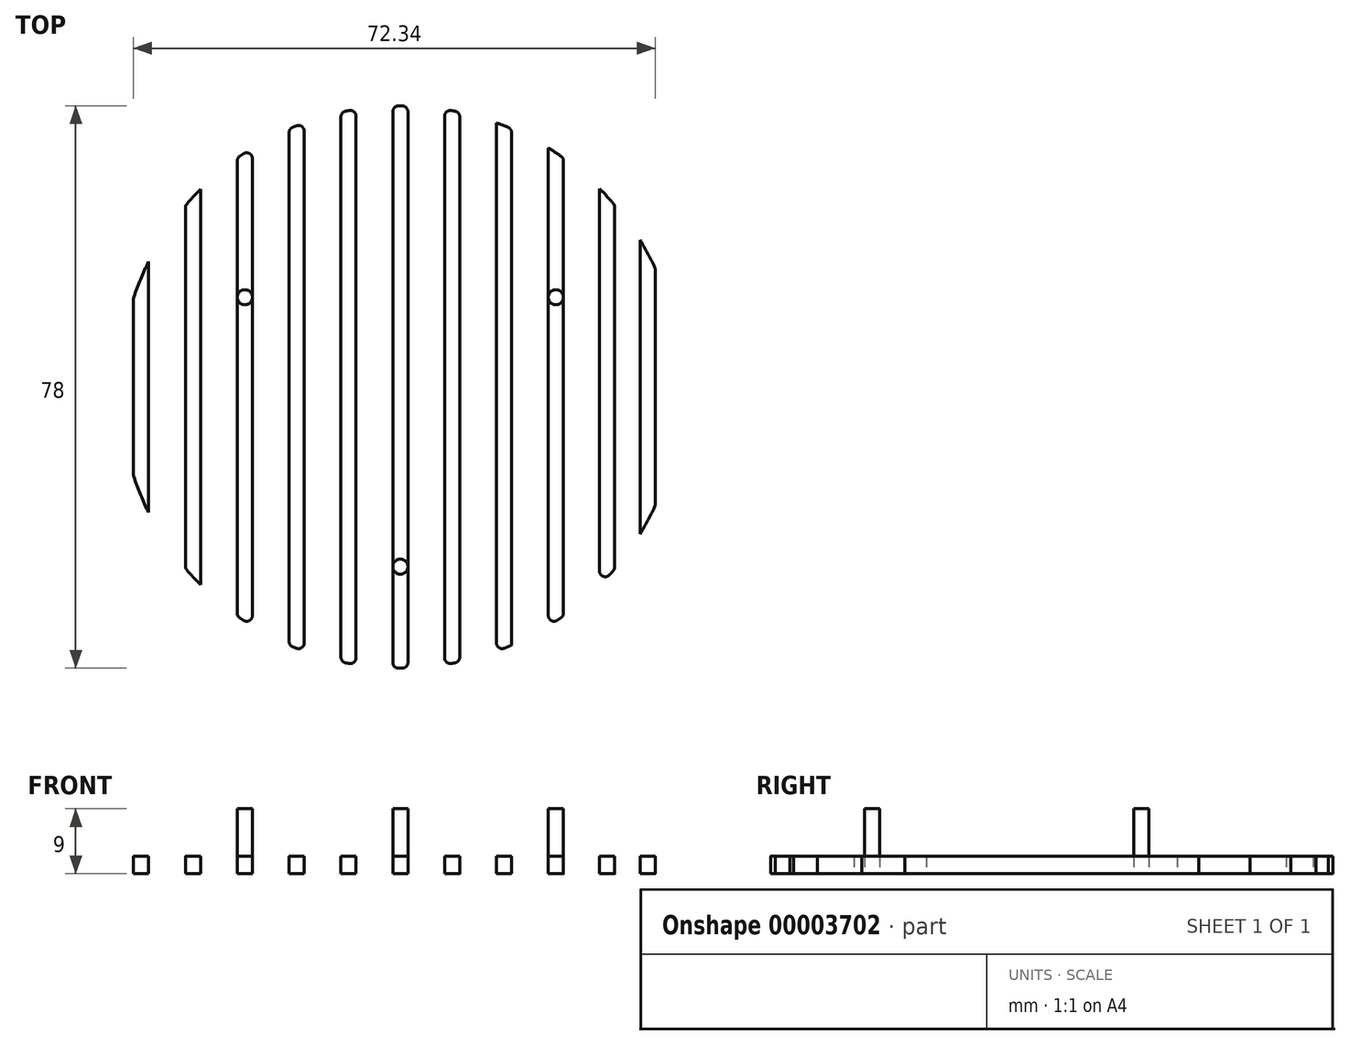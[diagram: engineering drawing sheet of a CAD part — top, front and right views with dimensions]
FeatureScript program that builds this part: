
annotation { "Feature Type Name" : "Feature", "Feature Type Description" : "" }
export const myFeature = defineFeature(function(context is Context, id is Id, definition is map)
    precondition{}
    {
        {
            var Q0;
            Q0=qCreatedBy(makeId("Top.planeOp"),FACE);
            var sketch = newSketch(context, id + "F0", { "sketchPlane" : qUnion([Q0])});
            skCircle(sketch, "E0", {"center": v(0, 0) * mm, "radius": 39 * mm});
            skCircle(sketch, "E1", {"center": v(0, -24.91) * mm, "radius": 1.05 * mm});
            skCircle(sketch, "E2.1.0", {"center": v(21.57, 12.46) * mm, "radius": 1.05 * mm});
            skCircle(sketch, "E2.2.0", {"center": v(-21.57, 12.46) * mm, "radius": 1.05 * mm});
            skLineSegment(sketch, "E3", {"start": v(-1.05, -24.91) * mm, "end": v(-1.05, 38.99) * mm});
            skLineSegment(sketch, "E4", {"start": v(1.05, -24.91) * mm, "end": v(1.05, 38.99) * mm});
            skLineSegment(sketch, "E5", {"start": v(-1.05, -24.91) * mm, "end": v(-1.05, -38.99) * mm});
            skLineSegment(sketch, "E6", {"start": v(1.05, -24.91) * mm, "end": v(1.05, -38.99) * mm});
            skLineSegment(sketch, "E7", {"start": v(-22.62, 12.46) * mm, "end": v(-22.62, 31.77) * mm});
            skLineSegment(sketch, "E8", {"start": v(-20.52, 12.46) * mm, "end": v(-20.52, 33.16) * mm});
            skLineSegment(sketch, "E9", {"start": v(-22.62, 12.46) * mm, "end": v(-22.62, -31.77) * mm});
            skLineSegment(sketch, "E10", {"start": v(-20.52, 12.46) * mm, "end": v(-20.52, -33.16) * mm});
            skLineSegment(sketch, "E11", {"start": v(-20.52, -33.16) * mm, "end": v(-19.7, -33.83) * mm});
            skLineSegment(sketch, "E12", {"start": v(20.52, 12.46) * mm, "end": v(20.52, 33.16) * mm});
            skLineSegment(sketch, "E13", {"start": v(22.62, 12.46) * mm, "end": v(22.62, 31.77) * mm});
            skLineSegment(sketch, "E14", {"start": v(20.52, 12.46) * mm, "end": v(20.52, -33.16) * mm});
            skLineSegment(sketch, "E15", {"start": v(22.62, 12.46) * mm, "end": v(22.62, -31.77) * mm});
            skCircle(sketch, "E16", {"center": v(0, 0) * mm, "radius": 41.1 * mm});
            skLineSegment(sketch, "E17", {"start": v(-15.43, 35.82) * mm, "end": v(-15.43, -35.82) * mm});
            skLineSegment(sketch, "E18", {"start": v(-13.33, 36.65) * mm, "end": v(-13.33, -36.65) * mm});
            skLineSegment(sketch, "E19", {"start": v(-8.24, 38.12) * mm, "end": v(-8.24, -38.12) * mm});
            skLineSegment(sketch, "E20", {"start": v(-6.14, 38.51) * mm, "end": v(-6.14, -38.12) * mm});
            skLineSegment(sketch, "E21", {"start": v(-20.52, 0) * mm, "end": v(-15.43, 0) * mm});
            skLineSegment(sketch, "E22", {"start": v(-13.33, 0) * mm, "end": v(-8.24, 0) * mm});
            skLineSegment(sketch, "E23", {"start": v(-6.14, 0) * mm, "end": v(-1.05, 0) * mm});
            skLineSegment(sketch, "E24", {"start": v(-27.71, 27.44) * mm, "end": v(-27.71, -27.44) * mm});
            skLineSegment(sketch, "E25", {"start": v(-29.81, 25.14) * mm, "end": v(-29.81, -25.14) * mm});
            skLineSegment(sketch, "E26", {"start": v(-34.9, 17.4) * mm, "end": v(-34.9, -17.4) * mm});
            skLineSegment(sketch, "E27", {"start": v(-37, 12.32) * mm, "end": v(-37, -12.32) * mm});
            skLineSegment(sketch, "E28", {"start": v(-22.62, 0) * mm, "end": v(-27.71, 0) * mm});
            skLineSegment(sketch, "E29", {"start": v(-29.81, 0) * mm, "end": v(-34.9, 0) * mm});
            skLineSegment(sketch, "E30", {"start": v(-6.14, -38.12) * mm, "end": v(-6.14, -38.51) * mm});
            skLineSegment(sketch, "E31", {"start": v(6.14, 38.51) * mm, "end": v(6.14, -38.51) * mm});
            skLineSegment(sketch, "E32", {"start": v(8.24, 38.12) * mm, "end": v(8.24, -38.12) * mm});
            skLineSegment(sketch, "E33", {"start": v(13.33, 36.65) * mm, "end": v(13.33, -36.65) * mm});
            skLineSegment(sketch, "E34", {"start": v(15.43, 35.82) * mm, "end": v(15.43, -35.82) * mm});
            skLineSegment(sketch, "E35", {"start": v(1.05, 0) * mm, "end": v(6.14, 0) * mm});
            skLineSegment(sketch, "E36", {"start": v(8.24, 0) * mm, "end": v(13.33, 0) * mm});
            skLineSegment(sketch, "E37", {"start": v(15.43, 0) * mm, "end": v(20.52, 0) * mm});
            skLineSegment(sketch, "E38", {"start": v(27.63, 27.53) * mm, "end": v(27.63, -27.53) * mm});
            skLineSegment(sketch, "E39", {"start": v(29.73, 25.25) * mm, "end": v(29.73, -25.25) * mm});
            skLineSegment(sketch, "E40", {"start": v(33.24, 20.4) * mm, "end": v(33.24, -20.4) * mm});
            skLineSegment(sketch, "E41", {"start": v(35.34, 16.5) * mm, "end": v(35.34, -16.5) * mm});
            skLineSegment(sketch, "E42", {"start": v(22.62, 0) * mm, "end": v(27.63, 0) * mm});
            skLineSegment(sketch, "E43", {"start": v(29.73, 0) * mm, "end": v(33.24, 0) * mm});
            skLineSegment(sketch, "E44", {"start": v(35.49, 0) * mm, "end": v(39, 0) * mm});
            skSolve(sketch);
        }
        {
            var Q0;
            {var subQ0=sQuery(id+"F0.wireOp",EDGE,"E2.2.0");var subQ2=makeQuery(id+"F0.imprint","INTERSECT",VERTEX,{"derivedFrom":[subQ0,sQuery(id+"F0.wireOp",EDGE,"E7"),sQuery(id+"F0.wireOp",EDGE,"E9")]});Q0=makeQuery(id+"F0.imprint","IMPRINT",FACE,{"disambiguationData":[TD([[makeQuery(id+"F0.imprint","IMPRINT",EDGE,{"disambiguationData":[TD([[subQ2,1.0]])],"derivedFrom":subQ0}),1.0]])]});}
            var Q1;
            {var subQ0=sQuery(id+"F0.wireOp",EDGE,"E2.1.0");var subQ2=makeQuery(id+"F0.imprint","INTERSECT",VERTEX,{"derivedFrom":[subQ0,sQuery(id+"F0.wireOp",EDGE,"E12"),sQuery(id+"F0.wireOp",EDGE,"E14")]});Q1=makeQuery(id+"F0.imprint","IMPRINT",FACE,{"disambiguationData":[TD([[makeQuery(id+"F0.imprint","IMPRINT",EDGE,{"disambiguationData":[TD([[subQ2,-1.0]])],"derivedFrom":subQ0}),1.0]])]});}
            var Q2;
            {var subQ0=sQuery(id+"F0.wireOp",EDGE,"E1");var subQ2=makeQuery(id+"F0.imprint","INTERSECT",VERTEX,{"derivedFrom":[subQ0,sQuery(id+"F0.wireOp",EDGE,"E3"),sQuery(id+"F0.wireOp",EDGE,"E5")]});Q2=makeQuery(id+"F0.imprint","IMPRINT",FACE,{"disambiguationData":[TD([[makeQuery(id+"F0.imprint","IMPRINT",EDGE,{"disambiguationData":[TD([[subQ2,1.0]])],"derivedFrom":subQ0}),1.0]])]});}
            extrude(context, id + "F1", {"entities" : qUnion([Q0, Q1, Q2]), "depth" : 9 * mm});
        }
        {
            var Q0;
            {var subQ0=sQuery(id+"F0.wireOp",EDGE,"E11");Q0=makeQuery(id+"F0.imprint","IMPRINT",FACE,{"disambiguationData":[TD([[makeQuery(id+"F0.imprint","IMPRINT",EDGE,{"derivedFrom":subQ0}),1.0]])]});}
            var Q1;
            {var subQ0=sQuery(id+"F0.wireOp",EDGE,"E27");Q1=makeQuery(id+"F0.imprint","IMPRINT",FACE,{"disambiguationData":[TD([[makeQuery(id+"F0.imprint","IMPRINT",EDGE,{"derivedFrom":subQ0}),1.0]])]});}
            var Q2;
            {var subQ2=sQuery(id+"F0.wireOp",EDGE,"E0");var subQ5=sQuery(id+"F0.wireOp",EDGE,"E24");var subQ8=makeQuery(id+"F0.imprint","INTERSECT",VERTEX,{"disambiguationData":[OD(0.0)],"derivedFrom":[subQ2,subQ5]});Q2=makeQuery(id+"F0.imprint","IMPRINT",FACE,{"disambiguationData":[TD([[makeQuery(id+"F0.imprint","IMPRINT",EDGE,{"disambiguationData":[TD([[subQ8,-1.0]])],"derivedFrom":subQ2}),1.0]])]});}
            var Q3;
            {var subQ2=sQuery(id+"F0.wireOp",EDGE,"E0");var subQ6=sQuery(id+"F0.wireOp",EDGE,"E9");var subQ8=makeQuery(id+"F0.imprint","INTERSECT",VERTEX,{"derivedFrom":[subQ2,subQ6]});Q3=makeQuery(id+"F0.imprint","IMPRINT",FACE,{"disambiguationData":[TD([[makeQuery(id+"F0.imprint","IMPRINT",EDGE,{"disambiguationData":[TD([[subQ8,1.0]])],"derivedFrom":subQ6}),1.0]])]});}
            var Q4;
            {var subQ2=sQuery(id+"F0.wireOp",EDGE,"E0");var subQ4=sQuery(id+"F0.wireOp",EDGE,"E17");var subQ7=makeQuery(id+"F0.imprint","INTERSECT",VERTEX,{"disambiguationData":[OD(0.0)],"derivedFrom":[subQ2,subQ4]});Q4=makeQuery(id+"F0.imprint","IMPRINT",FACE,{"disambiguationData":[TD([[makeQuery(id+"F0.imprint","IMPRINT",EDGE,{"disambiguationData":[TD([[subQ7,1.0]])],"derivedFrom":subQ2}),1.0]])]});}
            var Q5;
            {var subQ0=sQuery(id+"F0.wireOp",EDGE,"E30");Q5=makeQuery(id+"F0.imprint","IMPRINT",FACE,{"disambiguationData":[TD([[makeQuery(id+"F0.imprint","IMPRINT",EDGE,{"derivedFrom":subQ0}),-1.0]])]});}
            var Q6;
            {var subQ1=sQuery(id+"F0.wireOp",EDGE,"E7");Q6=makeQuery(id+"F0.imprint","IMPRINT",FACE,{"disambiguationData":[TD([[makeQuery(id+"F0.imprint","IMPRINT",EDGE,{"derivedFrom":subQ1}),-1.0]])]});}
            var Q7;
            {var subQ0=sQuery(id+"F0.wireOp",EDGE,"E2.2.0");var subQ2=makeQuery(id+"F0.imprint","INTERSECT",VERTEX,{"derivedFrom":[subQ0,sQuery(id+"F0.wireOp",EDGE,"E7"),sQuery(id+"F0.wireOp",EDGE,"E9")]});Q7=makeQuery(id+"F0.imprint","IMPRINT",FACE,{"disambiguationData":[TD([[makeQuery(id+"F0.imprint","IMPRINT",EDGE,{"disambiguationData":[TD([[subQ2,1.0]])],"derivedFrom":subQ0}),1.0]])]});}
            var Q8;
            {var subQ2=sQuery(id+"F0.wireOp",EDGE,"E0");var subQ6=sQuery(id+"F0.wireOp",EDGE,"E3");var subQ9=makeQuery(id+"F0.imprint","INTERSECT",VERTEX,{"derivedFrom":[subQ2,subQ6]});Q8=makeQuery(id+"F0.imprint","IMPRINT",FACE,{"disambiguationData":[TD([[makeQuery(id+"F0.imprint","IMPRINT",EDGE,{"disambiguationData":[TD([[subQ9,1.0]])],"derivedFrom":subQ2}),1.0]])]});}
            var Q9;
            {var subQ0=sQuery(id+"F0.wireOp",EDGE,"E1");var subQ2=makeQuery(id+"F0.imprint","INTERSECT",VERTEX,{"derivedFrom":[subQ0,sQuery(id+"F0.wireOp",EDGE,"E3"),sQuery(id+"F0.wireOp",EDGE,"E5")]});Q9=makeQuery(id+"F0.imprint","IMPRINT",FACE,{"disambiguationData":[TD([[makeQuery(id+"F0.imprint","IMPRINT",EDGE,{"disambiguationData":[TD([[subQ2,1.0]])],"derivedFrom":subQ0}),1.0]])]});}
            var Q10;
            {var subQ1=sQuery(id+"F0.wireOp",EDGE,"E5");Q10=makeQuery(id+"F0.imprint","IMPRINT",FACE,{"disambiguationData":[TD([[makeQuery(id+"F0.imprint","IMPRINT",EDGE,{"derivedFrom":subQ1}),1.0]])]});}
            var Q11;
            {var subQ2=sQuery(id+"F0.wireOp",EDGE,"E0");var subQ5=sQuery(id+"F0.wireOp",EDGE,"E31");var subQ8=makeQuery(id+"F0.imprint","INTERSECT",VERTEX,{"disambiguationData":[OD(0.0)],"derivedFrom":[subQ2,subQ5]});Q11=makeQuery(id+"F0.imprint","IMPRINT",FACE,{"disambiguationData":[TD([[makeQuery(id+"F0.imprint","IMPRINT",EDGE,{"disambiguationData":[TD([[subQ8,1.0]])],"derivedFrom":subQ2}),1.0]])]});}
            var Q12;
            {var subQ2=sQuery(id+"F0.wireOp",EDGE,"E0");var subQ4=sQuery(id+"F0.wireOp",EDGE,"E33");var subQ7=makeQuery(id+"F0.imprint","INTERSECT",VERTEX,{"disambiguationData":[OD(0.0)],"derivedFrom":[subQ2,subQ4]});Q12=makeQuery(id+"F0.imprint","IMPRINT",FACE,{"disambiguationData":[TD([[makeQuery(id+"F0.imprint","IMPRINT",EDGE,{"disambiguationData":[TD([[subQ7,1.0]])],"derivedFrom":subQ2}),1.0]])]});}
            var Q13;
            {var subQ2=sQuery(id+"F0.wireOp",EDGE,"E0");var subQ6=sQuery(id+"F0.wireOp",EDGE,"E14");var subQ8=makeQuery(id+"F0.imprint","INTERSECT",VERTEX,{"derivedFrom":[subQ2,subQ6]});Q13=makeQuery(id+"F0.imprint","IMPRINT",FACE,{"disambiguationData":[TD([[makeQuery(id+"F0.imprint","IMPRINT",EDGE,{"disambiguationData":[TD([[subQ8,-1.0]])],"derivedFrom":subQ2}),1.0]])]});}
            var Q14;
            {var subQ0=sQuery(id+"F0.wireOp",EDGE,"E2.1.0");var subQ2=makeQuery(id+"F0.imprint","INTERSECT",VERTEX,{"derivedFrom":[subQ0,sQuery(id+"F0.wireOp",EDGE,"E12"),sQuery(id+"F0.wireOp",EDGE,"E14")]});Q14=makeQuery(id+"F0.imprint","IMPRINT",FACE,{"disambiguationData":[TD([[makeQuery(id+"F0.imprint","IMPRINT",EDGE,{"disambiguationData":[TD([[subQ2,-1.0]])],"derivedFrom":subQ0}),1.0]])]});}
            var Q15;
            {var subQ1=sQuery(id+"F0.wireOp",EDGE,"E12");Q15=makeQuery(id+"F0.imprint","IMPRINT",FACE,{"disambiguationData":[TD([[makeQuery(id+"F0.imprint","IMPRINT",EDGE,{"derivedFrom":subQ1}),-1.0]])]});}
            var Q16;
            {var subQ2=sQuery(id+"F0.wireOp",EDGE,"E0");var subQ4=sQuery(id+"F0.wireOp",EDGE,"E38");var subQ8=makeQuery(id+"F0.imprint","INTERSECT",VERTEX,{"disambiguationData":[OD(0.0)],"derivedFrom":[subQ2,subQ4]});Q16=makeQuery(id+"F0.imprint","IMPRINT",FACE,{"disambiguationData":[TD([[makeQuery(id+"F0.imprint","IMPRINT",EDGE,{"disambiguationData":[TD([[subQ8,1.0]])],"derivedFrom":subQ2}),1.0]])]});}
            var Q17;
            {var subQ0=sQuery(id+"F0.wireOp",EDGE,"E41");Q17=makeQuery(id+"F0.imprint","IMPRINT",FACE,{"disambiguationData":[TD([[makeQuery(id+"F0.imprint","IMPRINT",EDGE,{"derivedFrom":subQ0}),-1.0]])]});}
            extrude(context, id + "F2", {"entities" : qUnion([Q0, Q1, Q2, Q3, Q4, Q5, Q6, Q7, Q8, Q9, Q10, Q11, Q12, Q13, Q14, Q15, Q16, Q17]), "depth" : 2.4 * mm});
        }
        {
            var Q0;
            Q0=makeQuery(id+"F2.opExtrude","SWEPT_EDGE",EDGE,{"disambiguationData":[OSD([sQuery(id+"F0.wireOp",EDGE,"E0"),sQuery(id+"F0.wireOp",EDGE,"E7")])]});
            var Q1;
            {var subQ0=sQuery(id+"F0.wireOp",EDGE,"E0");var subQ1=sQuery(id+"F0.wireOp",EDGE,"E17");Q1=makeQuery(id+"F2.opExtrude","SWEPT_EDGE",EDGE,{"disambiguationData":[OSD([subQ0,subQ1]),TDD([makeQuery(id+"F0.imprint","INTERSECT",VERTEX,{"disambiguationData":[OD(0.0)],"derivedFrom":[subQ0,subQ1]})])]});}
            var Q2;
            {var subQ0=sQuery(id+"F0.wireOp",EDGE,"E0");var subQ1=sQuery(id+"F0.wireOp",EDGE,"E19");Q2=makeQuery(id+"F2.opExtrude","SWEPT_EDGE",EDGE,{"disambiguationData":[OSD([subQ0,subQ1]),TDD([makeQuery(id+"F0.imprint","INTERSECT",VERTEX,{"disambiguationData":[OD(0.0)],"derivedFrom":[subQ0,subQ1]})])]});}
            var Q3;
            Q3=makeQuery(id+"F2.opExtrude","SWEPT_EDGE",EDGE,{"disambiguationData":[OSD([sQuery(id+"F0.wireOp",EDGE,"E0"),sQuery(id+"F0.wireOp",EDGE,"E3")])]});
            var Q4;
            Q4=makeQuery(id+"F2.opExtrude","SWEPT_EDGE",EDGE,{"disambiguationData":[OSD([sQuery(id+"F0.wireOp",EDGE,"E0"),sQuery(id+"F0.wireOp",EDGE,"E8")])]});
            var Q5;
            {var subQ0=sQuery(id+"F0.wireOp",EDGE,"E0");var subQ1=sQuery(id+"F0.wireOp",EDGE,"E18");Q5=makeQuery(id+"F2.opExtrude","SWEPT_EDGE",EDGE,{"disambiguationData":[OSD([subQ0,subQ1]),TDD([makeQuery(id+"F0.imprint","INTERSECT",VERTEX,{"disambiguationData":[OD(0.0)],"derivedFrom":[subQ0,subQ1]})])]});}
            var Q6;
            Q6=makeQuery(id+"F2.opExtrude","SWEPT_EDGE",EDGE,{"disambiguationData":[OSD([sQuery(id+"F0.wireOp",EDGE,"E0"),sQuery(id+"F0.wireOp",EDGE,"E20")])]});
            var Q7;
            Q7=makeQuery(id+"F2.opExtrude","SWEPT_EDGE",EDGE,{"disambiguationData":[OSD([sQuery(id+"F0.wireOp",EDGE,"E0"),sQuery(id+"F0.wireOp",EDGE,"E4")])]});
            var Q8;
            {var subQ0=sQuery(id+"F0.wireOp",EDGE,"E0");var subQ1=sQuery(id+"F0.wireOp",EDGE,"E31");Q8=makeQuery(id+"F2.opExtrude","SWEPT_EDGE",EDGE,{"disambiguationData":[OSD([subQ0,subQ1]),TDD([makeQuery(id+"F0.imprint","INTERSECT",VERTEX,{"disambiguationData":[OD(0.0)],"derivedFrom":[subQ0,subQ1]})])]});}
            var Q9;
            {var subQ0=sQuery(id+"F0.wireOp",EDGE,"E0");var subQ1=sQuery(id+"F0.wireOp",EDGE,"E32");Q9=makeQuery(id+"F2.opExtrude","SWEPT_EDGE",EDGE,{"disambiguationData":[OSD([subQ0,subQ1]),TDD([makeQuery(id+"F0.imprint","INTERSECT",VERTEX,{"disambiguationData":[OD(0.0)],"derivedFrom":[subQ0,subQ1]})])]});}
            var Q10;
            {var subQ0=sQuery(id+"F0.wireOp",EDGE,"E0");var subQ1=sQuery(id+"F0.wireOp",EDGE,"E34");Q10=makeQuery(id+"F2.opExtrude","SWEPT_EDGE",EDGE,{"disambiguationData":[OSD([subQ0,subQ1]),TDD([makeQuery(id+"F0.imprint","INTERSECT",VERTEX,{"disambiguationData":[OD(0.0)],"derivedFrom":[subQ0,subQ1]})])]});}
            var Q11;
            Q11=makeQuery(id+"F2.opExtrude","SWEPT_EDGE",EDGE,{"disambiguationData":[OSD([sQuery(id+"F0.wireOp",EDGE,"E0"),sQuery(id+"F0.wireOp",EDGE,"E13")])]});
            var Q12;
            {var subQ0=sQuery(id+"F0.wireOp",EDGE,"E0");var subQ1=sQuery(id+"F0.wireOp",EDGE,"E39");Q12=makeQuery(id+"F2.opExtrude","SWEPT_EDGE",EDGE,{"disambiguationData":[OSD([subQ0,subQ1]),TDD([makeQuery(id+"F0.imprint","INTERSECT",VERTEX,{"disambiguationData":[OD(0.0)],"derivedFrom":[subQ0,subQ1]})])]});}
            var Q13;
            {var subQ0=sQuery(id+"F0.wireOp",EDGE,"E0");var subQ1=sQuery(id+"F0.wireOp",EDGE,"E41");Q13=makeQuery(id+"F2.opExtrude","SWEPT_EDGE",EDGE,{"disambiguationData":[OSD([subQ0,subQ1]),TDD([makeQuery(id+"F0.imprint","INTERSECT",VERTEX,{"disambiguationData":[OD(0.0)],"derivedFrom":[subQ0,subQ1]})])]});}
            var Q14;
            {var subQ0=sQuery(id+"F0.wireOp",EDGE,"E0");var subQ1=sQuery(id+"F0.wireOp",EDGE,"E41");Q14=makeQuery(id+"F2.opExtrude","SWEPT_EDGE",EDGE,{"disambiguationData":[OSD([subQ0,subQ1]),TDD([makeQuery(id+"F0.imprint","INTERSECT",VERTEX,{"disambiguationData":[OD(1.0)],"derivedFrom":[subQ0,subQ1]})])]});}
            var Q15;
            {var subQ0=sQuery(id+"F0.wireOp",EDGE,"E0");var subQ1=sQuery(id+"F0.wireOp",EDGE,"E39");Q15=makeQuery(id+"F2.opExtrude","SWEPT_EDGE",EDGE,{"disambiguationData":[OSD([subQ0,subQ1]),TDD([makeQuery(id+"F0.imprint","INTERSECT",VERTEX,{"disambiguationData":[OD(1.0)],"derivedFrom":[subQ0,subQ1]})])]});}
            var Q16;
            Q16=makeQuery(id+"F2.opExtrude","SWEPT_EDGE",EDGE,{"disambiguationData":[OSD([sQuery(id+"F0.wireOp",EDGE,"E0"),sQuery(id+"F0.wireOp",EDGE,"E15")])]});
            var Q17;
            {var subQ0=sQuery(id+"F0.wireOp",EDGE,"E0");var subQ1=sQuery(id+"F0.wireOp",EDGE,"E38");Q17=makeQuery(id+"F2.opExtrude","SWEPT_EDGE",EDGE,{"disambiguationData":[OSD([subQ0,subQ1]),TDD([makeQuery(id+"F0.imprint","INTERSECT",VERTEX,{"disambiguationData":[OD(1.0)],"derivedFrom":[subQ0,subQ1]})])]});}
            var Q18;
            Q18=makeQuery(id+"F2.opExtrude","SWEPT_EDGE",EDGE,{"disambiguationData":[OSD([sQuery(id+"F0.wireOp",EDGE,"E0"),sQuery(id+"F0.wireOp",EDGE,"E14")])]});
            var Q19;
            {var subQ0=sQuery(id+"F0.wireOp",EDGE,"E0");var subQ1=sQuery(id+"F0.wireOp",EDGE,"E32");Q19=makeQuery(id+"F2.opExtrude","SWEPT_EDGE",EDGE,{"disambiguationData":[OSD([subQ0,subQ1]),TDD([makeQuery(id+"F0.imprint","INTERSECT",VERTEX,{"disambiguationData":[OD(1.0)],"derivedFrom":[subQ0,subQ1]})])]});}
            var Q20;
            Q20=makeQuery(id+"F2.opExtrude","SWEPT_EDGE",EDGE,{"disambiguationData":[OSD([sQuery(id+"F0.wireOp",EDGE,"E0"),sQuery(id+"F0.wireOp",EDGE,"E6")])]});
            var Q21;
            Q21=makeQuery(id+"F2.opExtrude","SWEPT_EDGE",EDGE,{"disambiguationData":[OSD([sQuery(id+"F0.wireOp",EDGE,"E0"),sQuery(id+"F0.wireOp",EDGE,"E30")])]});
            var Q22;
            {var subQ0=sQuery(id+"F0.wireOp",EDGE,"E0");var subQ1=sQuery(id+"F0.wireOp",EDGE,"E18");Q22=makeQuery(id+"F2.opExtrude","SWEPT_EDGE",EDGE,{"disambiguationData":[OSD([subQ0,subQ1]),TDD([makeQuery(id+"F0.imprint","INTERSECT",VERTEX,{"disambiguationData":[OD(1.0)],"derivedFrom":[subQ0,subQ1]})])]});}
            var Q23;
            Q23=makeQuery(id+"F2.opExtrude","SWEPT_EDGE",EDGE,{"disambiguationData":[OSD([sQuery(id+"F0.wireOp",EDGE,"E0"),sQuery(id+"F0.wireOp",EDGE,"E10"),sQuery(id+"F0.wireOp",EDGE,"E11")])]});
            var Q24;
            {var subQ0=sQuery(id+"F0.wireOp",EDGE,"E0");var subQ1=sQuery(id+"F0.wireOp",EDGE,"E33");Q24=makeQuery(id+"F2.opExtrude","SWEPT_EDGE",EDGE,{"disambiguationData":[OSD([subQ0,subQ1]),TDD([makeQuery(id+"F0.imprint","INTERSECT",VERTEX,{"disambiguationData":[OD(1.0)],"derivedFrom":[subQ0,subQ1]})])]});}
            var Q25;
            {var subQ0=sQuery(id+"F0.wireOp",EDGE,"E0");var subQ1=sQuery(id+"F0.wireOp",EDGE,"E31");Q25=makeQuery(id+"F2.opExtrude","SWEPT_EDGE",EDGE,{"disambiguationData":[OSD([subQ0,subQ1]),TDD([makeQuery(id+"F0.imprint","INTERSECT",VERTEX,{"disambiguationData":[OD(1.0)],"derivedFrom":[subQ0,subQ1]})])]});}
            var Q26;
            Q26=makeQuery(id+"F2.opExtrude","SWEPT_EDGE",EDGE,{"disambiguationData":[OSD([sQuery(id+"F0.wireOp",EDGE,"E0"),sQuery(id+"F0.wireOp",EDGE,"E5")])]});
            var Q27;
            {var subQ0=sQuery(id+"F0.wireOp",EDGE,"E0");var subQ1=sQuery(id+"F0.wireOp",EDGE,"E19");Q27=makeQuery(id+"F2.opExtrude","SWEPT_EDGE",EDGE,{"disambiguationData":[OSD([subQ0,subQ1]),TDD([makeQuery(id+"F0.imprint","INTERSECT",VERTEX,{"disambiguationData":[OD(1.0)],"derivedFrom":[subQ0,subQ1]})])]});}
            var Q28;
            {var subQ0=sQuery(id+"F0.wireOp",EDGE,"E0");var subQ1=sQuery(id+"F0.wireOp",EDGE,"E17");Q28=makeQuery(id+"F2.opExtrude","SWEPT_EDGE",EDGE,{"disambiguationData":[OSD([subQ0,subQ1]),TDD([makeQuery(id+"F0.imprint","INTERSECT",VERTEX,{"disambiguationData":[OD(1.0)],"derivedFrom":[subQ0,subQ1]})])]});}
            var Q29;
            Q29=makeQuery(id+"F2.opExtrude","SWEPT_EDGE",EDGE,{"disambiguationData":[OSD([sQuery(id+"F0.wireOp",EDGE,"E0"),sQuery(id+"F0.wireOp",EDGE,"E9")])]});
            var Q30;
            {var subQ0=sQuery(id+"F0.wireOp",EDGE,"E0");var subQ1=sQuery(id+"F0.wireOp",EDGE,"E25");Q30=makeQuery(id+"F2.opExtrude","SWEPT_EDGE",EDGE,{"disambiguationData":[OSD([subQ0,subQ1]),TDD([makeQuery(id+"F0.imprint","INTERSECT",VERTEX,{"disambiguationData":[OD(1.0)],"derivedFrom":[subQ0,subQ1]})])]});}
            var Q31;
            {var subQ0=sQuery(id+"F0.wireOp",EDGE,"E0");var subQ1=sQuery(id+"F0.wireOp",EDGE,"E27");Q31=makeQuery(id+"F2.opExtrude","SWEPT_EDGE",EDGE,{"disambiguationData":[OSD([subQ0,subQ1]),TDD([makeQuery(id+"F0.imprint","INTERSECT",VERTEX,{"disambiguationData":[OD(1.0)],"derivedFrom":[subQ0,subQ1]})])]});}
            var Q32;
            {var subQ0=sQuery(id+"F0.wireOp",EDGE,"E0");var subQ1=sQuery(id+"F0.wireOp",EDGE,"E27");Q32=makeQuery(id+"F2.opExtrude","SWEPT_EDGE",EDGE,{"disambiguationData":[OSD([subQ0,subQ1]),TDD([makeQuery(id+"F0.imprint","INTERSECT",VERTEX,{"disambiguationData":[OD(0.0)],"derivedFrom":[subQ0,subQ1]})])]});}
            var Q33;
            {var subQ0=sQuery(id+"F0.wireOp",EDGE,"E0");var subQ1=sQuery(id+"F0.wireOp",EDGE,"E25");Q33=makeQuery(id+"F2.opExtrude","SWEPT_EDGE",EDGE,{"disambiguationData":[OSD([subQ0,subQ1]),TDD([makeQuery(id+"F0.imprint","INTERSECT",VERTEX,{"disambiguationData":[OD(0.0)],"derivedFrom":[subQ0,subQ1]})])]});}
            fillet(context, id + "F3", {"entities" : qUnion([Q0, Q1, Q2, Q3, Q4, Q5, Q6, Q7, Q8, Q9, Q10, Q11, Q12, Q13, Q14, Q15, Q16, Q17, Q18, Q19, Q20, Q21, Q22, Q23, Q24, Q25, Q26, Q27, Q28, Q29, Q30, Q31, Q32, Q33]), "radius" : 0.8 * mm, "tangentPropagation" : true, "allowEdgeOverflow" : false});
        }
    });
